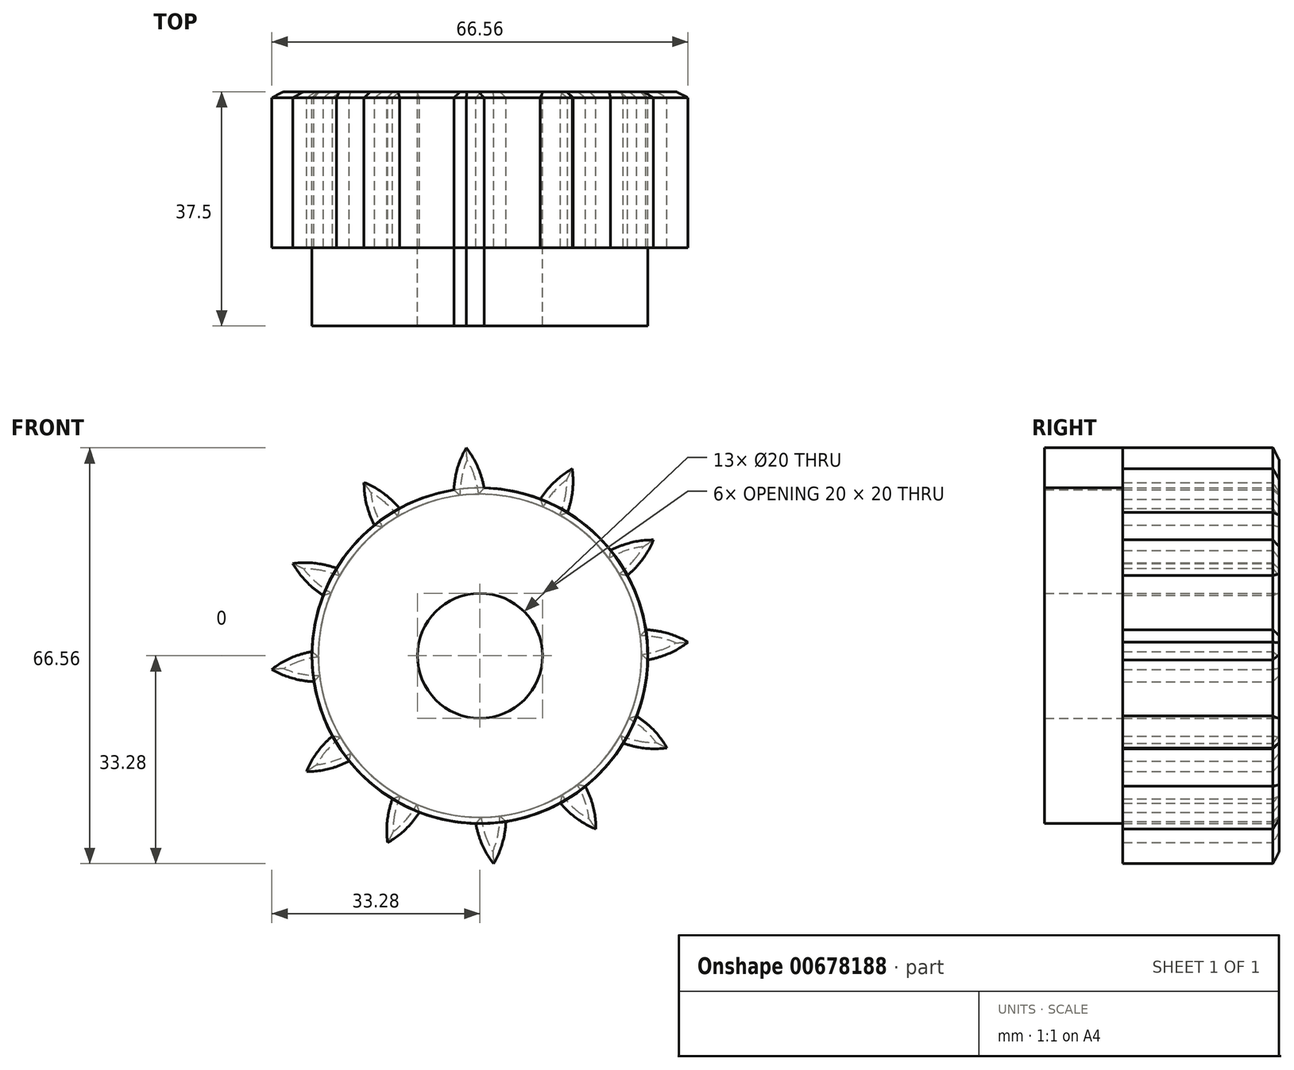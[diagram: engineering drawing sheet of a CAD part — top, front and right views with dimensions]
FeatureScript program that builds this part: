
annotation { "Feature Type Name" : "Feature", "Feature Type Description" : "" }
export const myFeature = defineFeature(function(context is Context, id is Id, definition is map)
    precondition{}
    {
        {
            var Q0;
            Q0=qCreatedBy(makeId("Front.planeOp"),FACE);
            var sketch = newSketch(context, id + "F0", { "sketchPlane" : qUnion([Q0])});
            skCircle(sketch, "E0", {"center": v(0, 0) * mm, "radius": 26.86 * mm});
            skCircle(sketch, "E1", {"center": v(0, 0) * mm, "radius": 29.32 * mm, "construction": true});
            skCircle(sketch, "E2", {"center": v(0, 0) * mm, "radius": 31.75 * mm, "construction": true});
            skLineSegment(sketch, "E3", {"start": v(0, 0) * mm, "end": v(0, 78.84) * mm, "construction": true});
            skLineSegment(sketch, "E4", {"start": v(0, 0) * mm, "end": v(-5.91, 90.2) * mm, "construction": true});
            skPoint(sketch, "E5.startSnap0", {"position": v(0, 39.42) * mm});
            skLineSegment(sketch, "E6", {"start": v(0, 29.32) * mm, "end": v(-64.13, 29.32) * mm, "construction": true});
            skLineSegment(sketch, "E7", {"start": v(0, 29.33) * mm, "end": v(-66.32, 5.19) * mm, "construction": true});
            skCircle(sketch, "E8", {"center": v(0, 0) * mm, "radius": 27.56 * mm, "construction": true});
            skCircle(sketch, "E9", {"center": v(0, 29.32) * mm, "radius": 14.6 * mm, "construction": true});
            skCircle(sketch, "E10", {"center": v(-13.72, 24.33) * mm, "radius": 14.6 * mm, "construction": true});
            skArc(sketch, "E11", {"start": v(0.66, 26.85) * mm, "mid": v(0.38, 28.1) * mm, "end": v(0, 29.32) * mm});
            skArc(sketch, "E12", {"start": v(0, 29.32) * mm, "mid": v(-1.1, 31.7) * mm, "end": v(-2.63, 33.83) * mm});
            skArc(sketch, "E13.MirrorCS", {"start": v(-3.83, 29.07) * mm, "mid": v(-3.04, 31.57) * mm, "end": v(-1.8, 33.88) * mm});
            skCircle(sketch, "E14.MirrorC", {"center": v(10.43, 25.91) * mm, "radius": 14.6 * mm, "construction": true});
            skArc(sketch, "E15.MirrorCS", {"start": v(-4.16, 26.54) * mm, "mid": v(-4.05, 27.81) * mm, "end": v(-3.83, 29.07) * mm});
            skArc(sketch, "E16", {"start": v(-2.63, 33.83) * mm, "mid": v(-2.22, 33.85) * mm, "end": v(-1.8, 33.88) * mm});
            skCircle(sketch, "E17", {"center": v(0, 0) * mm, "radius": 37.5 * mm});
            skSolve(sketch);
        }
        {
            var Q0;
            {var subQ0=sQuery(id+"F0.wireOp",EDGE,"E0");var subQ1=makeQuery(id+"F0.imprint","INTERSECT",VERTEX,{"derivedFrom":[subQ0,sQuery(id+"F0.wireOp",EDGE,"E11")]});Q0=makeQuery(id+"F0.imprint","IMPRINT",FACE,{"disambiguationData":[TD([[makeQuery(id+"F0.imprint","IMPRINT",EDGE,{"disambiguationData":[TD([[subQ1,-1.0]])],"derivedFrom":subQ0}),1.0]])]});}
            var Q1;
            {var subQ0=sQuery(id+"F0.wireOp",EDGE,"E11");Q1=makeQuery(id+"F0.imprint","IMPRINT",FACE,{"disambiguationData":[TD([[makeQuery(id+"F0.imprint","IMPRINT",EDGE,{"derivedFrom":subQ0}),1.0]])]});}
            extrude(context, id + "F1", {"entities" : qUnion([Q0, Q1]), "depth" : 25 * mm, "offsetDistance" : 25 * mm});
        }
        {
            var Q0;
            Q0=makeQuery(id+"F1.opExtrude","SWEPT_BODY",BODY,{"disambiguationData":[OSD([sQuery(id+"F0.wireOp",EDGE,"E0"),sQuery(id+"F0.wireOp",EDGE,"E11"),sQuery(id+"F0.wireOp",EDGE,"E12"),sQuery(id+"F0.wireOp",EDGE,"E13.MirrorCS"),sQuery(id+"F0.wireOp",EDGE,"E15.MirrorCS"),sQuery(id+"F0.wireOp",EDGE,"E16")])]});
            var Q1;
            Q1=makeQuery(id+"F1.opExtrude","SWEPT_FACE",FACE,{"disambiguationData":[OSD([sQuery(id+"F0.wireOp",EDGE,"E0")])]});
            circularPattern(context, id + "F2", {"entities" : qUnion([Q0]), "axis" : qUnion([Q1]), "angle" : 360 * degree, "instanceCount" : 12, "equalSpace" : true});
        }
        {
            var Q0;
            {var subQ0=sQuery(id+"F0.wireOp",EDGE,"E17");var subQ1=makeQuery(id+"F1.opExtrude","CAP_FACE",FACE,{"disambiguationData":[OSD([sQuery(id+"F0.wireOp",EDGE,"E0"),sQuery(id+"F0.wireOp",EDGE,"E11"),sQuery(id+"F0.wireOp",EDGE,"E12"),sQuery(id+"F0.wireOp",EDGE,"E13.MirrorCS"),sQuery(id+"F0.wireOp",EDGE,"E15.MirrorCS"),sQuery(id+"F0.wireOp",EDGE,"E16"),subQ0])],"isStart":true});Q0=makeQuery(id+"Fhplm4RGl4bD7Tf_1.boolean.opBoolean","MERGE",FACE,{"derivedFrom":[subQ1,makeQuery(id+"F2.opPattern","COPY",FACE,{"derivedFrom":subQ1,"instanceName":"1"}),makeQuery(id+"F2.opPattern","COPY",FACE,{"derivedFrom":subQ1,"instanceName":"2"}),makeQuery(id+"F2.opPattern","COPY",FACE,{"derivedFrom":subQ1,"instanceName":"3"}),makeQuery(id+"F2.opPattern","COPY",FACE,{"derivedFrom":subQ1,"instanceName":"4"}),makeQuery(id+"F2.opPattern","COPY",FACE,{"derivedFrom":subQ1,"instanceName":"5"}),makeQuery(id+"F2.opPattern","COPY",FACE,{"derivedFrom":subQ1,"instanceName":"6"}),makeQuery(id+"F2.opPattern","COPY",FACE,{"derivedFrom":subQ1,"instanceName":"7"}),makeQuery(id+"F2.opPattern","COPY",FACE,{"derivedFrom":subQ1,"instanceName":"8"}),makeQuery(id+"F2.opPattern","COPY",FACE,{"derivedFrom":subQ1,"instanceName":"9"}),makeQuery(id+"F2.opPattern","COPY",FACE,{"derivedFrom":subQ1,"instanceName":"10"}),makeQuery(id+"F2.opPattern","COPY",FACE,{"derivedFrom":subQ1,"instanceName":"11"}),makeQuery(id+"F2.opPattern","COPY",FACE,{"derivedFrom":subQ1,"instanceName":"12"}),makeQuery(id+"F2.opPattern","COPY",FACE,{"derivedFrom":subQ1,"instanceName":"13"}),makeQuery(id+"F2.opPattern","COPY",FACE,{"derivedFrom":subQ1,"instanceName":"14"}),makeQuery(id+"F2.opPattern","COPY",FACE,{"derivedFrom":subQ1,"instanceName":"15"}),makeQuery(id+"F2.opPattern","COPY",FACE,{"derivedFrom":subQ1,"instanceName":"16"}),makeQuery(id+"F2.opPattern","COPY",FACE,{"derivedFrom":subQ1,"instanceName":"17"}),makeQuery(id+"F2.opPattern","COPY",FACE,{"derivedFrom":subQ1,"instanceName":"18"}),makeQuery(id+"F2.opPattern","COPY",FACE,{"derivedFrom":subQ1,"instanceName":"19"}),makeQuery(id+"F2.opPattern","COPY",FACE,{"derivedFrom":subQ1,"instanceName":"20"}),makeQuery(id+"F2.opPattern","COPY",FACE,{"derivedFrom":subQ1,"instanceName":"21"}),makeQuery(id+"F2.opPattern","COPY",FACE,{"derivedFrom":subQ1,"instanceName":"22"}),makeQuery(id+"F2.opPattern","COPY",FACE,{"derivedFrom":subQ1,"instanceName":"23"}),makeQuery(id+"Fhplm4RGl4bD7Tf_1.opExtrude","CAP_FACE",FACE,{"disambiguationData":[OSD([subQ0,sQuery(id+"F0.wireOp",EDGE,"qpPqxLE5-FOOR-wDck-a7wx-b4TQk7TcEIHh"),sQuery(id+"F0.wireOp",EDGE,"eH8ngF4i-G9Ao-5fsW-YTaq-L8gvtuLGUVGT"),sQuery(id+"F0.wireOp",EDGE,"RZBC8zmN-9yTC-7Cw9-tZBY-7Sipv5iGPh4E"),sQuery(id+"F0.wireOp",EDGE,"CS9RCDur-1nFA-4qDE-vtJY-lhLShyDcuL6u"),sQuery(id+"F0.wireOp",EDGE,"SORVajN9-ghQI-2ZGS-ScmT-HEAKRttnpEe7")])],"isStart":true})]});}
            chamfer(context, id + "F3", {"entities" : qUnion([Q0]), "width" : 1 * mm, "tangentPropagation" : true});
        }
        {
            var Q0;
            Q0=sQuery(id+"F0.wireOp",VERTEX,"E3.start");
            var Q1;
            Q1=makeQuery(id+"F1.opExtrude","SWEPT_BODY",BODY,{"disambiguationData":[OSD([sQuery(id+"F0.wireOp",EDGE,"E0"),sQuery(id+"F0.wireOp",EDGE,"E11"),sQuery(id+"F0.wireOp",EDGE,"E12"),sQuery(id+"F0.wireOp",EDGE,"E13.MirrorCS"),sQuery(id+"F0.wireOp",EDGE,"E15.MirrorCS")])]});
            var Q2;
            Q2=makeQuery(id+"F2.opPattern","COPY",BODY,{"derivedFrom":makeQuery(id+"F1.opExtrude","SWEPT_BODY",BODY,{"disambiguationData":[OSD([sQuery(id+"F0.wireOp",EDGE,"E0"),sQuery(id+"F0.wireOp",EDGE,"E11"),sQuery(id+"F0.wireOp",EDGE,"E12"),sQuery(id+"F0.wireOp",EDGE,"E13.MirrorCS"),sQuery(id+"F0.wireOp",EDGE,"E15.MirrorCS")])]}),"instanceName":"1"});
            var Q3;
            Q3=makeQuery(id+"F2.opPattern","COPY",BODY,{"derivedFrom":makeQuery(id+"F1.opExtrude","SWEPT_BODY",BODY,{"disambiguationData":[OSD([sQuery(id+"F0.wireOp",EDGE,"E0"),sQuery(id+"F0.wireOp",EDGE,"E11"),sQuery(id+"F0.wireOp",EDGE,"E12"),sQuery(id+"F0.wireOp",EDGE,"E13.MirrorCS"),sQuery(id+"F0.wireOp",EDGE,"E15.MirrorCS")])]}),"instanceName":"2"});
            var Q4;
            Q4=makeQuery(id+"F2.opPattern","COPY",BODY,{"derivedFrom":makeQuery(id+"F1.opExtrude","SWEPT_BODY",BODY,{"disambiguationData":[OSD([sQuery(id+"F0.wireOp",EDGE,"E0"),sQuery(id+"F0.wireOp",EDGE,"E11"),sQuery(id+"F0.wireOp",EDGE,"E12"),sQuery(id+"F0.wireOp",EDGE,"E13.MirrorCS"),sQuery(id+"F0.wireOp",EDGE,"E15.MirrorCS")])]}),"instanceName":"3"});
            var Q5;
            Q5=makeQuery(id+"F2.opPattern","COPY",BODY,{"derivedFrom":makeQuery(id+"F1.opExtrude","SWEPT_BODY",BODY,{"disambiguationData":[OSD([sQuery(id+"F0.wireOp",EDGE,"E0"),sQuery(id+"F0.wireOp",EDGE,"E11"),sQuery(id+"F0.wireOp",EDGE,"E12"),sQuery(id+"F0.wireOp",EDGE,"E13.MirrorCS"),sQuery(id+"F0.wireOp",EDGE,"E15.MirrorCS")])]}),"instanceName":"4"});
            var Q6;
            Q6=makeQuery(id+"F2.opPattern","COPY",BODY,{"derivedFrom":makeQuery(id+"F1.opExtrude","SWEPT_BODY",BODY,{"disambiguationData":[OSD([sQuery(id+"F0.wireOp",EDGE,"E0"),sQuery(id+"F0.wireOp",EDGE,"E11"),sQuery(id+"F0.wireOp",EDGE,"E12"),sQuery(id+"F0.wireOp",EDGE,"E13.MirrorCS"),sQuery(id+"F0.wireOp",EDGE,"E15.MirrorCS")])]}),"instanceName":"5"});
            var Q7;
            Q7=makeQuery(id+"F2.opPattern","COPY",BODY,{"derivedFrom":makeQuery(id+"F1.opExtrude","SWEPT_BODY",BODY,{"disambiguationData":[OSD([sQuery(id+"F0.wireOp",EDGE,"E0"),sQuery(id+"F0.wireOp",EDGE,"E11"),sQuery(id+"F0.wireOp",EDGE,"E12"),sQuery(id+"F0.wireOp",EDGE,"E13.MirrorCS"),sQuery(id+"F0.wireOp",EDGE,"E15.MirrorCS")])]}),"instanceName":"6"});
            var Q8;
            Q8=makeQuery(id+"F2.opPattern","COPY",BODY,{"derivedFrom":makeQuery(id+"F1.opExtrude","SWEPT_BODY",BODY,{"disambiguationData":[OSD([sQuery(id+"F0.wireOp",EDGE,"E0"),sQuery(id+"F0.wireOp",EDGE,"E11"),sQuery(id+"F0.wireOp",EDGE,"E12"),sQuery(id+"F0.wireOp",EDGE,"E13.MirrorCS"),sQuery(id+"F0.wireOp",EDGE,"E15.MirrorCS")])]}),"instanceName":"7"});
            var Q9;
            Q9=makeQuery(id+"F2.opPattern","COPY",BODY,{"derivedFrom":makeQuery(id+"F1.opExtrude","SWEPT_BODY",BODY,{"disambiguationData":[OSD([sQuery(id+"F0.wireOp",EDGE,"E0"),sQuery(id+"F0.wireOp",EDGE,"E11"),sQuery(id+"F0.wireOp",EDGE,"E12"),sQuery(id+"F0.wireOp",EDGE,"E13.MirrorCS"),sQuery(id+"F0.wireOp",EDGE,"E15.MirrorCS")])]}),"instanceName":"8"});
            var Q10;
            Q10=makeQuery(id+"F2.opPattern","COPY",BODY,{"derivedFrom":makeQuery(id+"F1.opExtrude","SWEPT_BODY",BODY,{"disambiguationData":[OSD([sQuery(id+"F0.wireOp",EDGE,"E0"),sQuery(id+"F0.wireOp",EDGE,"E11"),sQuery(id+"F0.wireOp",EDGE,"E12"),sQuery(id+"F0.wireOp",EDGE,"E13.MirrorCS"),sQuery(id+"F0.wireOp",EDGE,"E15.MirrorCS")])]}),"instanceName":"9"});
            var Q11;
            Q11=makeQuery(id+"F2.opPattern","COPY",BODY,{"derivedFrom":makeQuery(id+"F1.opExtrude","SWEPT_BODY",BODY,{"disambiguationData":[OSD([sQuery(id+"F0.wireOp",EDGE,"E0"),sQuery(id+"F0.wireOp",EDGE,"E11"),sQuery(id+"F0.wireOp",EDGE,"E12"),sQuery(id+"F0.wireOp",EDGE,"E13.MirrorCS"),sQuery(id+"F0.wireOp",EDGE,"E15.MirrorCS")])]}),"instanceName":"10"});
            var Q12;
            Q12=makeQuery(id+"F2.opPattern","COPY",BODY,{"derivedFrom":makeQuery(id+"F1.opExtrude","SWEPT_BODY",BODY,{"disambiguationData":[OSD([sQuery(id+"F0.wireOp",EDGE,"E0"),sQuery(id+"F0.wireOp",EDGE,"E11"),sQuery(id+"F0.wireOp",EDGE,"E12"),sQuery(id+"F0.wireOp",EDGE,"E13.MirrorCS"),sQuery(id+"F0.wireOp",EDGE,"E15.MirrorCS")])]}),"instanceName":"11"});
            hole(context, id + "F4", {"style" : HoleStyle.SIMPLE, "endStyle" : HoleEndStyle.THROUGH, "oppositeDirection" : true, "holeDiameter" : 20 * mm, "majorDiameter" : 5 * mm, "isTappedThrough" : true, "tappedDepth" : 12 * mm, "tapClearance" : 3, "locations" : qUnion([Q0]), "scope" : qUnion([Q1, Q2, Q3, Q4, Q5, Q6, Q7, Q8, Q9, Q10, Q11, Q12])});
        }
        {
            var Q0;
            Q0=makeQuery(id+"F1.opExtrude","CAP_FACE",FACE,{"disambiguationData":[OSD([sQuery(id+"F0.wireOp",EDGE,"E0"),sQuery(id+"F0.wireOp",EDGE,"E11"),sQuery(id+"F0.wireOp",EDGE,"E12"),sQuery(id+"F0.wireOp",EDGE,"E13.MirrorCS"),sQuery(id+"F0.wireOp",EDGE,"E15.MirrorCS")])],"isStart":false});
            extrude(context, id + "F5", {"entities" : qUnion([Q0]), "depth" : 12.5 * mm, "offsetDistance" : 25 * mm});
        }
    });
